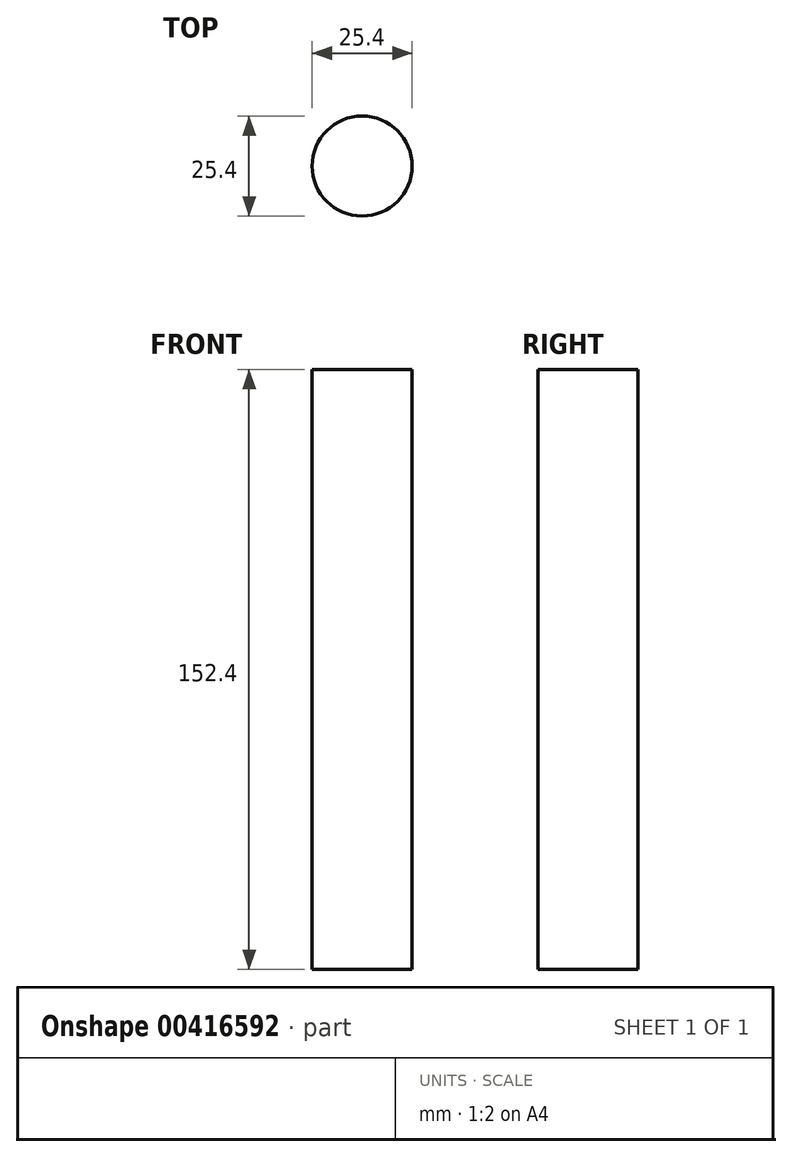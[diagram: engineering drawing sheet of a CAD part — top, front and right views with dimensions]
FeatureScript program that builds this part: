
annotation { "Feature Type Name" : "Feature", "Feature Type Description" : "" }
export const myFeature = defineFeature(function(context is Context, id is Id, definition is map)
    precondition{}
    {
        {
            var Q0;
            Q0=qCreatedBy(makeId("Top.planeOp"),FACE);
            var sketch = newSketch(context, id + "F0", { "sketchPlane" : qUnion([Q0])});
            skCircle(sketch, "E0", {"center": v(0, 0) * mm, "radius": 12.7 * mm});
            skSolve(sketch);
        }
        {
            var Q0;
            Q0 = qSketchRegion(id + "F0", true);
            extrude(context, id + "F1", {"entities" : qUnion([Q0]), "depth" : 152.4 * mm, "offsetDistance" : 25.4 * mm});
        }
    });
